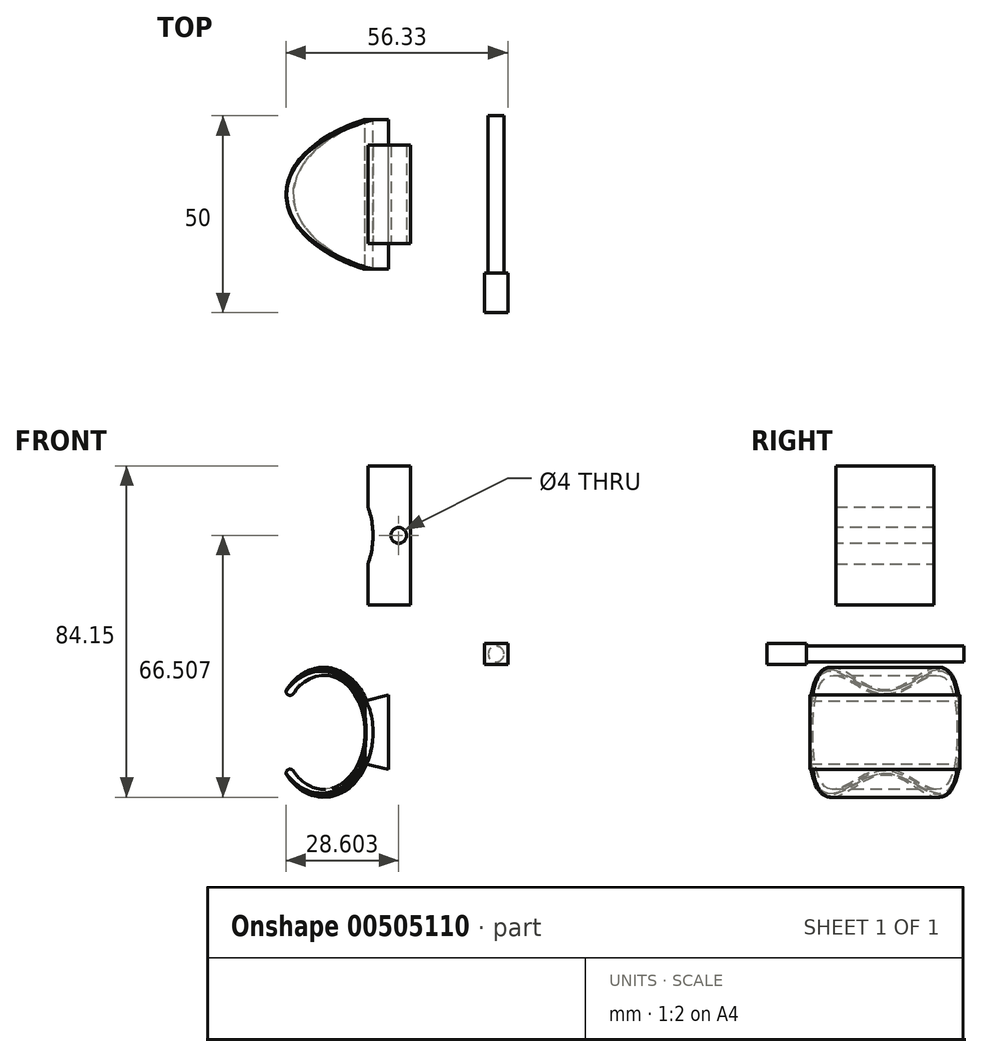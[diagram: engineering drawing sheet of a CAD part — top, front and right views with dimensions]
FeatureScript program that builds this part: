
annotation { "Feature Type Name" : "Feature", "Feature Type Description" : "" }
export const myFeature = defineFeature(function(context is Context, id is Id, definition is map)
    precondition{}
    {
        {
            var Q0;
            Q0=qCreatedBy(makeId("Front.planeOp"),FACE);
            var sketch = newSketch(context, id + "F0", { "sketchPlane" : qUnion([Q0])});
            skEllipse(sketch, "E0", {"center": v(0, 0) * mm, "majorRadius": 16.5 * mm, "minorRadius": 12.5 * mm, "majorAxis": v(0, 1)});
            skEllipse(sketch, "E1", {"center": v(0, 0) * mm, "majorRadius": 14.5 * mm, "minorRadius": 10.5 * mm, "majorAxis": v(0, -1)});
            skSolve(sketch);
        }
        {
            var Q0;
            Q0=makeQuery(id+"F0.imprint","IMPRINT",FACE,{"disambiguationData":[TD([[makeQuery(id+"F0.imprint","IMPRINT",EDGE,{"derivedFrom":sQuery(id+"F0.wireOp",EDGE,"E0")}),1.0]])]});
            extrude(context, id + "F1", {"entities" : qUnion([Q0]), "depth" : 39.5 * mm, "symmetric" : true});
        }
        {
            var Q0;
            Q0=qCreatedBy(makeId("Top.planeOp"),FACE);
            var sketch = newSketch(context, id + "F2", { "sketchPlane" : qUnion([Q0])});
            skEllipse(sketch, "E2", {"center": v(30.5, 0) * mm, "majorRadius": 40.06 * mm, "minorRadius": 22 * mm, "majorAxis": v(-1, 0)});
            skSolve(sketch);
        }
        {
            var Q0;
            Q0=makeQuery(id+"F2.imprint","IMPRINT",FACE,{"disambiguationData":[TD([[makeQuery(id+"F2.imprint","IMPRINT",EDGE,{"derivedFrom":sQuery(id+"F2.wireOp",EDGE,"E2")}),1.0]])]});
            extrude(context, id + "F3", {"entities" : qUnion([Q0]), "depth" : 40 * mm, "symmetric" : true});
        }
        {
            var Q0;
            Q0=makeQuery(id+"F1.opExtrude","SWEPT_BODY",BODY,{"disambiguationData":[OSD([sQuery(id+"F0.wireOp",EDGE,"E0"),sQuery(id+"F0.wireOp",EDGE,"E1")])]});
            var Q1;
            Q1=makeQuery(id+"F3.opExtrude","SWEPT_BODY",BODY,{"disambiguationData":[OSD([sQuery(id+"F2.wireOp",EDGE,"E2")])]});
            booleanBodies(context, id + "F4", {"operationType" : BooleanOperationType.INTERSECTION, "tools" : qUnion([Q0, Q1])});
        }
        {
            var Q0;
            Q0=makeQuery(id+"F4.opBoolean","INTERSECT",EDGE,{"derivedFrom":[makeQuery(id+"F1.opExtrude","SWEPT_FACE",FACE,{"disambiguationData":[OSD([sQuery(id+"F0.wireOp",EDGE,"E1")])]}),makeQuery(id+"F3.opExtrude","SWEPT_FACE",FACE,{"disambiguationData":[OSD([sQuery(id+"F2.wireOp",EDGE,"E2")])]})]});
            fillet(context, id + "F5", {"entities" : qUnion([Q0]), "radius" : 1 * mm, "tangentPropagation" : true, "allowEdgeOverflow" : false});
        }
        {
            var Q0;
            Q0=makeQuery(id+"F4.opBoolean","INTERSECT",EDGE,{"derivedFrom":[makeQuery(id+"F1.opExtrude","SWEPT_FACE",FACE,{"disambiguationData":[OSD([sQuery(id+"F0.wireOp",EDGE,"E0")])]}),makeQuery(id+"F3.opExtrude","SWEPT_FACE",FACE,{"disambiguationData":[OSD([sQuery(id+"F2.wireOp",EDGE,"E2")])]})]});
            fillet(context, id + "F6", {"entities" : qUnion([Q0]), "radius" : 0.5 * mm, "tangentPropagation" : true, "allowEdgeOverflow" : false});
        }
        {
            var Q0;
            Q0=qCreatedBy(makeId("Front.planeOp"),FACE);
            var sketch = newSketch(context, id + "F7", { "sketchPlane" : qUnion([Q0])});
            skLineSegment(sketch, "E3.left", {"start": v(10.5, -8) * mm, "end": v(10.5, 8) * mm});
            skLineSegment(sketch, "E3.right", {"start": v(16.5, -9.5) * mm, "end": v(16.5, 9.5) * mm});
            skPoint(sketch, "E3.middle", {"position": v(13.5, 0) * mm});
            skLineSegment(sketch, "E4", {"start": v(16.5, 9.5) * mm, "end": v(10.5, 8) * mm});
            skLineSegment(sketch, "E5", {"start": v(16.5, -9.5) * mm, "end": v(10.5, -8) * mm});
            skPoint(sketch, "E6.orphan", {"position": v(10.5, 9.5) * mm});
            skPoint(sketch, "E3.bottom.start.orphan", {"position": v(10.5, -9.5) * mm});
            skSolve(sketch);
        }
        {
            var Q0;
            Q0=makeQuery(id+"F7.imprint","IMPRINT",FACE,{"disambiguationData":[TD([[makeQuery(id+"F7.imprint","IMPRINT",EDGE,{"derivedFrom":sQuery(id+"F7.wireOp",EDGE,"E3.left")}),-1.0]])]});
            extrude(context, id + "F8", {"entities" : qUnion([Q0]), "depth" : 38 * mm, "symmetric" : true});
        }
        {
            var Q0;
            Q0=makeQuery(id+"F8.opExtrude","SWEPT_FACE",FACE,{"disambiguationData":[OSD([sQuery(id+"F7.wireOp",EDGE,"E3.right")])]});
            var sketch = newSketch(context, id + "F9", { "sketchPlane" : qUnion([Q0])});
            skLineSegment(sketch, "E7.bottom", {"start": v(19, -19.93) * mm, "end": v(-19, -19.93) * mm});
            skLineSegment(sketch, "E7.top", {"start": v(19, 19.93) * mm, "end": v(-19, 19.93) * mm});
            skLineSegment(sketch, "E7.left", {"start": v(19, -19.93) * mm, "end": v(19, 19.93) * mm});
            skLineSegment(sketch, "E7.right", {"start": v(-19, -19.93) * mm, "end": v(-19, 19.93) * mm});
            skPoint(sketch, "E7.middle", {"position": v(0, 0) * mm});
            skSolve(sketch);
        }
        {
            var Q0;
            {var subQ0=sQuery(id+"F9.wireOp",EDGE,"E7.top");Q0=makeQuery(id+"F9.imprint","IMPRINT",FACE,{"disambiguationData":[TD([[makeQuery(id+"F9.imprint","IMPRINT",EDGE,{"derivedFrom":subQ0}),1.0]])]});}
            var Q1;
            {var subQ1=sQuery(id+"F7.wireOp",EDGE,"E3.right");var subQ2=makeQuery(id+"F8.opExtrude","SWEPT_EDGE",EDGE,{"disambiguationData":[OSD([subQ1,sQuery(id+"F7.wireOp",EDGE,"E5")])]});Q1=makeQuery(id+"F9.imprint","IMPRINT",FACE,{"disambiguationData":[TD([[makeQuery(id+"F9.imprint","IMPRINT",EDGE,{"derivedFrom":subQ2}),1.0]])]});}
            var Q2;
            {var subQ0=sQuery(id+"F9.wireOp",EDGE,"E7.bottom");Q2=makeQuery(id+"F9.imprint","IMPRINT",FACE,{"disambiguationData":[TD([[makeQuery(id+"F9.imprint","IMPRINT",EDGE,{"derivedFrom":subQ0}),-1.0]])]});}
            extrude(context, id + "F10", {"entities" : qUnion([Q0, Q1, Q2]), "oppositeDirection" : true, "depth" : 40 * mm});
        }
        {
            var Q0;
            Q0=makeQuery(id+"F10.opExtrude","SWEPT_BODY",BODY,{"disambiguationData":[OSD([sQuery(id+"F9.wireOp",EDGE,"E7.bottom"),sQuery(id+"F9.wireOp",EDGE,"E7.top"),sQuery(id+"F9.wireOp",EDGE,"E7.left"),sQuery(id+"F9.wireOp",EDGE,"E7.right")])]});
            var Q1;
            Q1=makeQuery(id+"F4.opBoolean","INTERSECT",BODY,{"derivedFrom":[makeQuery(id+"F1.opExtrude","SWEPT_BODY",BODY,{"disambiguationData":[OSD([sQuery(id+"F0.wireOp",EDGE,"E0"),sQuery(id+"F0.wireOp",EDGE,"E1")])]}),makeQuery(id+"F3.opExtrude","SWEPT_BODY",BODY,{"disambiguationData":[OSD([sQuery(id+"F2.wireOp",EDGE,"E2")])]})]});
            booleanBodies(context, id + "F11", {"operationType" : BooleanOperationType.INTERSECTION, "tools" : qUnion([Q0, Q1])});
        }
        {
            var Q0;
            Q0=makeQuery(id+"F11.opBoolean","INTERSECT",BODY,{"derivedFrom":[makeQuery(id+"F4.opBoolean","INTERSECT",BODY,{"derivedFrom":[makeQuery(id+"F1.opExtrude","SWEPT_BODY",BODY,{"disambiguationData":[OSD([sQuery(id+"F0.wireOp",EDGE,"E0"),sQuery(id+"F0.wireOp",EDGE,"E1")])]}),makeQuery(id+"F3.opExtrude","SWEPT_BODY",BODY,{"disambiguationData":[OSD([sQuery(id+"F2.wireOp",EDGE,"E2")])]})]}),makeQuery(id+"F10.opExtrude","SWEPT_BODY",BODY,{"disambiguationData":[OSD([sQuery(id+"F9.wireOp",EDGE,"E7.bottom"),sQuery(id+"F9.wireOp",EDGE,"E7.top"),sQuery(id+"F9.wireOp",EDGE,"E7.left"),sQuery(id+"F9.wireOp",EDGE,"E7.right")])]})]});
            var Q1;
            Q1=makeQuery(id+"F8.opExtrude","CAP_EDGE",EDGE,{"disambiguationData":[OSD([sQuery(id+"F7.wireOp",EDGE,"E3.left")])],"isStart":false});
            var Q2;
            Q2=makeQuery(id+"F8.opExtrude","CAP_EDGE",EDGE,{"disambiguationData":[OSD([sQuery(id+"F7.wireOp",EDGE,"E3.left")])],"isStart":false});
            transform(context, id + "F12", {"entities" : qUnion([Q0]), "transformType" : TransformType.TRANSLATION_DISTANCE, "transformDirection" : qUnion([Q2]), "distance" : 50 * mm, "makeCopy" : true});
        }
        {
            var Q0;
            Q0=qCreatedBy(makeId("Front.planeOp"),FACE);
            var sketch = newSketch(context, id + "F13", { "sketchPlane" : qUnion([Q0])});
            skLineSegment(sketch, "E8.bottom", {"start": v(11.22, 32.36) * mm, "end": v(22.02, 32.36) * mm});
            skLineSegment(sketch, "E8.top", {"start": v(11.22, 67.65) * mm, "end": v(22.02, 67.65) * mm});
            skLineSegment(sketch, "E8.left", {"start": v(11.22, 32.36) * mm, "end": v(11.22, 67.65) * mm});
            skLineSegment(sketch, "E8.right", {"start": v(22.02, 32.36) * mm, "end": v(22.02, 67.65) * mm});
            skSolve(sketch);
        }
        {
            var Q0;
            Q0=makeQuery(id+"F13.imprint","IMPRINT",FACE,{"disambiguationData":[TD([[makeQuery(id+"F13.imprint","IMPRINT",EDGE,{"derivedFrom":sQuery(id+"F13.wireOp",EDGE,"E8.bottom")}),1.0]])]});
            extrude(context, id + "F14", {"entities" : qUnion([Q0]), "depth" : 25 * mm, "offsetDistance" : 25 * mm, "symmetric" : true});
        }
        {
            var Q0;
            Q0=makeQuery(id+"F12.opPattern","COPY",BODY,{"derivedFrom":makeQuery(id+"F11.opBoolean","INTERSECT",BODY,{"derivedFrom":[makeQuery(id+"F4.opBoolean","INTERSECT",BODY,{"derivedFrom":[makeQuery(id+"F1.opExtrude","SWEPT_BODY",BODY,{"disambiguationData":[OSD([sQuery(id+"F0.wireOp",EDGE,"E0"),sQuery(id+"F0.wireOp",EDGE,"E1")])]}),makeQuery(id+"F3.opExtrude","SWEPT_BODY",BODY,{"disambiguationData":[OSD([sQuery(id+"F2.wireOp",EDGE,"E2")])]})]}),makeQuery(id+"F10.opExtrude","SWEPT_BODY",BODY,{"disambiguationData":[OSD([sQuery(id+"F9.wireOp",EDGE,"E7.bottom"),sQuery(id+"F9.wireOp",EDGE,"E7.top"),sQuery(id+"F9.wireOp",EDGE,"E7.left"),sQuery(id+"F9.wireOp",EDGE,"E7.right")])]})]}),"instanceName":"1"});
            var Q1;
            Q1=makeQuery(id+"F14.opExtrude","SWEPT_BODY",BODY,{"disambiguationData":[OSD([sQuery(id+"F13.wireOp",EDGE,"E8.bottom"),sQuery(id+"F13.wireOp",EDGE,"E8.top"),sQuery(id+"F13.wireOp",EDGE,"E8.left"),sQuery(id+"F13.wireOp",EDGE,"E8.right")])]});
            booleanBodies(context, id + "F15", {"operationType" : BooleanOperationType.SUBTRACTION, "tools" : qUnion([Q0]), "targets" : qUnion([Q1])});
        }
        {
            var Q0;
            Q0=makeQuery(id+"F14.opExtrude","CAP_FACE",FACE,{"disambiguationData":[OSD([sQuery(id+"F13.wireOp",EDGE,"E8.bottom"),sQuery(id+"F13.wireOp",EDGE,"E8.top"),sQuery(id+"F13.wireOp",EDGE,"E8.left"),sQuery(id+"F13.wireOp",EDGE,"E8.right")])],"isStart":false});
            var sketch = newSketch(context, id + "F16", { "sketchPlane" : qUnion([Q0])});
            skLineSegment(sketch, "E9", {"start": v(22.02, 50) * mm, "end": v(16.5, 50) * mm});
            skCircle(sketch, "E10", {"center": v(19.04, 50) * mm, "radius": 2 * mm});
            skSolve(sketch);
        }
        {
            var Q0;
            Q0=sQuery(id+"F16.wireOp",VERTEX,"E10.center");
            var Q1;
            Q1=makeQuery(id+"F14.opExtrude","SWEPT_BODY",BODY,{"disambiguationData":[OSD([sQuery(id+"F13.wireOp",EDGE,"E8.bottom"),sQuery(id+"F13.wireOp",EDGE,"E8.top"),sQuery(id+"F13.wireOp",EDGE,"E8.left"),sQuery(id+"F13.wireOp",EDGE,"E8.right")])]});
            hole(context, id + "F17", {"style" : HoleStyle.SIMPLE, "endStyle" : HoleEndStyle.THROUGH, "holeDiameter" : 4 * mm, "majorDiameter" : 5 * mm, "isTappedThrough" : true, "tappedDepth" : 12 * mm, "tapClearance" : 3, "locations" : qUnion([Q0]), "scope" : qUnion([Q1])});
        }
        {
            var Q0;
            Q0=qCreatedBy(makeId("Front.planeOp"),FACE);
            var sketch = newSketch(context, id + "F18", { "sketchPlane" : qUnion([Q0])});
            skCircle(sketch, "E11", {"center": v(43.78, 19.89) * mm, "radius": 2 * mm});
            skSolve(sketch);
        }
        {
            var Q0;
            Q0=makeQuery(id+"F18.imprint","IMPRINT",FACE,{"disambiguationData":[TD([[makeQuery(id+"F18.imprint","IMPRINT",EDGE,{"derivedFrom":sQuery(id+"F18.wireOp",EDGE,"E11")}),1.0]])]});
            extrude(context, id + "F19", {"entities" : qUnion([Q0]), "depth" : 40 * mm, "offsetDistance" : 25 * mm, "symmetric" : true});
        }
        {
            var Q0;
            Q0=makeQuery(id+"F19.opExtrude","CAP_FACE",FACE,{"disambiguationData":[OSD([sQuery(id+"F18.wireOp",EDGE,"E11")])],"isStart":false});
            var sketch = newSketch(context, id + "F20", { "sketchPlane" : qUnion([Q0])});
            skLineSegment(sketch, "E12.bottom", {"start": v(40.8, 22.5) * mm, "end": v(46.77, 22.5) * mm});
            skLineSegment(sketch, "E12.top", {"start": v(40.8, 17.27) * mm, "end": v(46.77, 17.27) * mm});
            skLineSegment(sketch, "E12.left", {"start": v(40.8, 22.5) * mm, "end": v(40.8, 17.27) * mm});
            skLineSegment(sketch, "E12.right", {"start": v(46.77, 22.5) * mm, "end": v(46.77, 17.27) * mm});
            skPoint(sketch, "E12.middle", {"position": v(43.78, 19.89) * mm});
            skSolve(sketch);
        }
        {
            var Q0;
            Q0=makeQuery(id+"F20.imprint","IMPRINT",FACE,{"disambiguationData":[TD([[makeQuery(id+"F20.imprint","IMPRINT",EDGE,{"derivedFrom":sQuery(id+"F20.wireOp",EDGE,"E12.bottom")}),-1.0]])]});
            var Q1;
            Q1=makeQuery(id+"F20.imprint","IMPRINT",FACE,{"disambiguationData":[TD([[makeQuery(id+"F20.imprint","IMPRINT",EDGE,{"derivedFrom":makeQuery(id+"F19.opExtrude","CAP_EDGE",EDGE,{"disambiguationData":[OSD([sQuery(id+"F18.wireOp",EDGE,"E11")])],"isStart":false})}),1.0]])]});
            extrude(context, id + "F21", {"entities" : qUnion([Q0, Q1]), "operationType" : NewBodyOperationType.ADD, "depth" : 10 * mm, "offsetDistance" : 25 * mm});
        }
    });
